# Revit family: pfav-xp224_560dmj_60Hz
name_source: partatom
category: 機械設備
units: mm (PartAtom-declared; Revit-internal decimal feet)

## family parameters
OmniClass タイトル = Split System Air Conditioning Units
OmniClass 番号 = 23.75.10.24.21.27.27
パーツ タイプ = 標準
ロード時にボイドで切り取り = いいえ
丸型コネクタ寸法 = 直径を使用
作業面ベース = いいえ
共有 = いいえ
常に垂直 = はい
部屋計算ポイント = いいえ

## types (4) — shared parameters
Clearance Back = 50  [stored 0.164042 ft]
Clearance Front = 800  [stored 2.62467 ft]
Clearance Left = 100  [stored 0.328084 ft]
Clearance Right = 100  [stored 0.328084 ft]
Clearance Top = 1000  [stored 3.28084 ft]
IfcExportAs = IfcUnitaryEquipmentType
IfcExportType = AIRCONDITIONINGUNIT
OmniClassCode = 23-33 17 13 11
S寸法 = 150
URL = https://www.mitsubishielectric.co.jp
Uniclass2015Code = Pr_70_65_03_84
Uniclass2015Title = Split coil remote air cooled condensing units
Uniclass2015Version = Systems v1.9
サービススペース = はい
ドレン管径 = 34.00 mm
仕様書バージョン = Version1.0
企業コード = 108420
冷媒液管径 = 12.70 mm
冷媒管径 = 100.00 mm
冷媒高低圧ガス管径 = 0.00 mm
分類コード = 50053003023020
加湿給水管径 = 27.00 mm
参照している仕様書等のバージョン = 公共建築工事標準仕様書（機械設備工事編）平成31年度版
周波数 = 60 Hz
呼称 = パッケージ形空気調和機_室内機
始動方式 = 直入
形式 = 床置（露出）立形
推奨ブレーカー容量 = 15 A
暖房能力 = 0 kW
最小電線太さ_mm2 = 1.6
本体マテリアル = <カテゴリ別>
極数 = 3
機外静圧 = 30.0 Pa
法定耐用年数 = 15
消費電力_加湿器 = 0 W
消費電力_電気ヒーター = 0 W
相 = 3
相_電気ヒーター = 1
積算_科目 = 1 空気調和設備
符号 = PAC-FRV(J)
製品リリース年月 = 2018年10月10日
製品出荷対象 = 国内
製造元 = 三菱電機株式会社
設置方法 = 床置形
説明 = 設備用パッケージエアコン 空冷床置形・冷暖兼用 ファシレアＤＤリプレースタイプ
負荷分類 = 3_ファン類
運転質量 = 0.00 kg
電動機出力_圧縮機 = 0 W
電圧 = 200 V
電圧_電気ヒーター = 0 V
zero-valued in all types: APF, COP, 価格, 有効加湿量, 機械基礎_D, 機械基礎_H, 機械基礎_W

## per-type parameters (varying)
| type | Depth | Height | MAX風量 | Width | ダクト幅 | ダクト高 | 冷媒ガス管径 | 冷媒管径符号 | 冷房能力 | 形名 | 最大電流値 | 消費電力 | 消費電力_冷房 | 消費電力_暖房 | 製品質量 | 質量 | 電動機出力_送風機 | 音響パワーレベル(dB) | 風量 | 風量（m3／min） |
| PFAV-XP280DMJ | 485  [stored 1.59121 ft] | 1750  [stored 5.74147 ft] | 5400.0 m³/h | 980  [stored 3.21522 ft] | 715 mm | 334 mm | 22.20 mm | Cf | 25 kW | PFAV-XP-DMJ : PFAV-XP280DMJ1 | 6 A | 1150 W | 1150 W | 1150 W | 140.00 kg | 168.00 kg | 1200 W | 76 | 5400.0 m³/h | 90 |
| PFAV-XP450DMJ | 635 | 1900 | 8400.0 m³/h | 1200 | 1046 mm | 489 mm | 19.05 mm | Ce | 40 kW | PFAV-XP-DMJ : PFAV-XP450DMJ1 | 10 A | 1400 W | 1400 W | 1400 W | 238.00 kg | 285.60 kg | 2400 W | 76 | 8400.0 m³/h | 140 |
| PFAV-XP224DMJ | 485  [stored 1.59121 ft] | 1750  [stored 5.74147 ft] | 3900.0 m³/h | 980  [stored 3.21522 ft] | 715 mm | 334 mm | 19.05 mm | Ce | 20 kW | PFAV-XP-DMJ : PFAV-XP224DMJ1 | 6 A | 510 W | 510 W | 510 W | 136.00 kg | 163.20 kg | 1200 W | 68 | 3900.0 m³/h | 65 |
| PFAV-XP560DMJ | 635 | 1900 | 9900.0 m³/h | 1200 | 1046 mm | 489 mm | 22.20 mm | Cf | 50 kW | PFAV-XP-DMJ : PFAV-XP560DMJ1 | 10 A | 1780 W | 1780 W | 1780 W | 238.00 kg | 285.60 kg | 2400 W | 79 | 9900.0 m³/h | 165 |

note: column(s) folded — value = type name in every type: モデル

note: [stored X ft] marks values corroborated as IEEE doubles in the binary element streams (Revit-internal decimal feet)

## geometry (parser evidence)
native form markers: Blend x2
no freeform markers — native parametric forms only
